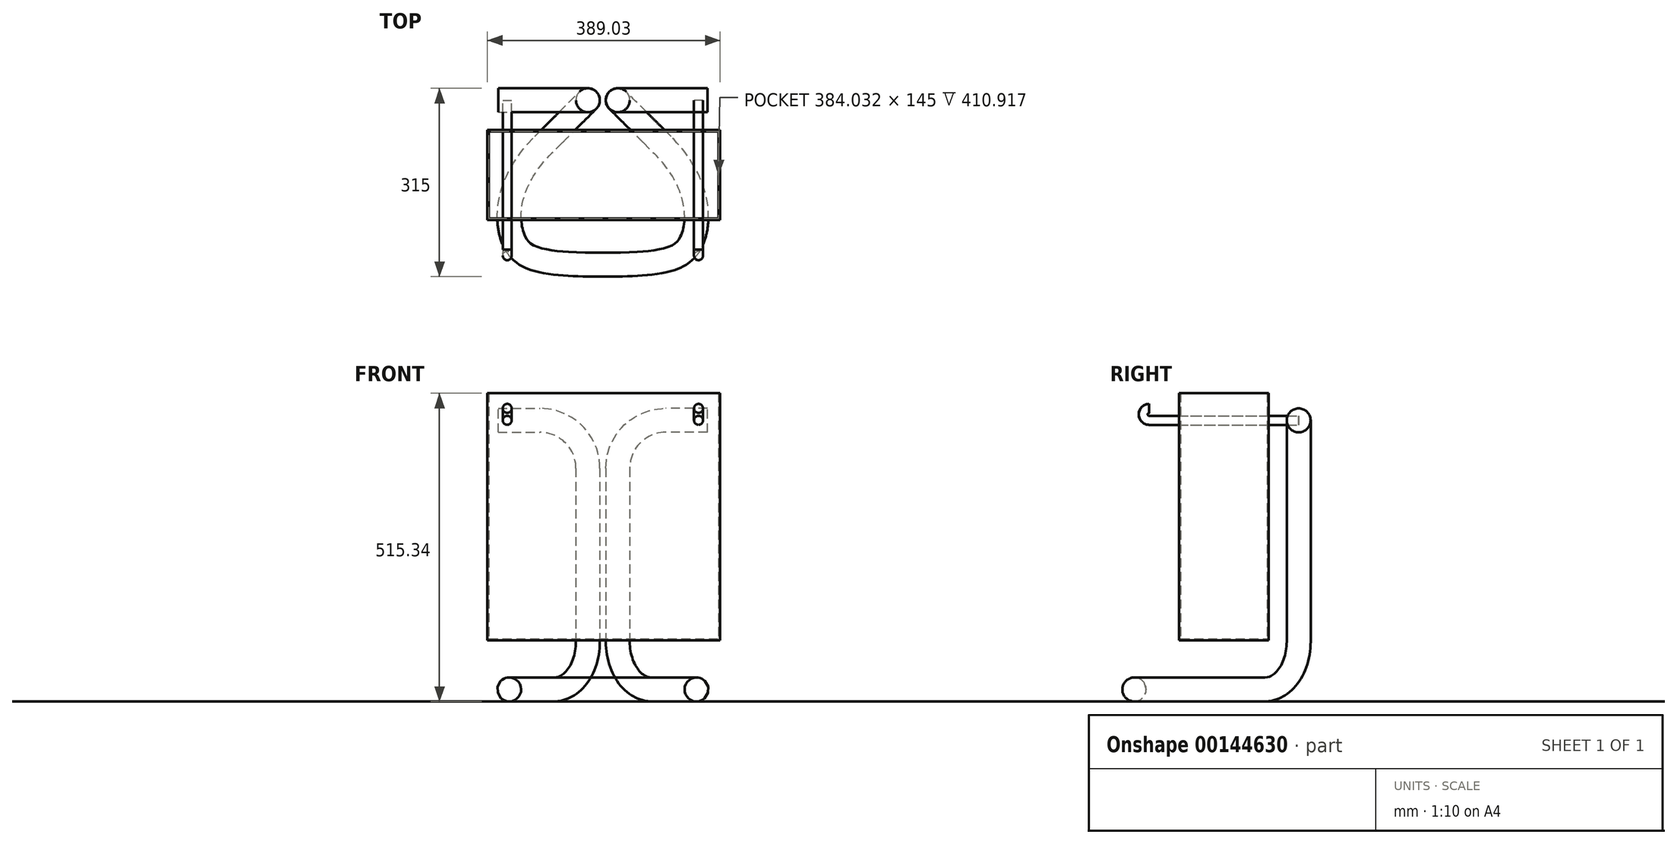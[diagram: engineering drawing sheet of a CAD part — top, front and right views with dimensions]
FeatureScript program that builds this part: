
annotation { "Feature Type Name" : "Feature", "Feature Type Description" : "" }
export const myFeature = defineFeature(function(context is Context, id is Id, definition is map)
    precondition{}
    {
        {
            var Q0;
            Q0=qCreatedBy(makeId("Top.planeOp"),FACE);
            var sketch = newSketch(context, id + "F0", { "sketchPlane" : qUnion([Q0])});
            skLineSegment(sketch, "E0.bottom", {"start": v(-150, 150) * mm, "end": v(150, 150) * mm, "construction": true});
            skLineSegment(sketch, "E0.top", {"start": v(-150, -150) * mm, "end": v(150, -150) * mm, "construction": true});
            skLineSegment(sketch, "E0.left", {"start": v(-150, 150) * mm, "end": v(-150, -150) * mm, "construction": true});
            skLineSegment(sketch, "E0.right", {"start": v(150, 150) * mm, "end": v(150, -150) * mm, "construction": true});
            skPoint(sketch, "E0.middle", {"position": v(0, 0) * mm});
            skLineSegment(sketch, "E1", {"start": v(0, 150) * mm, "end": v(0, -150) * mm, "construction": true});
            skFitSpline(sketch, "E2", {"points": [v(0, -150) * mm, v(150, -106.6) * mm, v(100, 50) * mm], "startDerivative": vector(649.1, 0) * mm, "endDerivative": vector(-356.53, 356.53) * mm});
            skLineSegment(sketch, "E3", {"start": v(0, 50) * mm, "end": v(100, 50) * mm, "construction": true});
            skLineSegment(sketch, "E4", {"start": v(100, 50) * mm, "end": v(100, 150) * mm, "construction": true});
            skLineSegment(sketch, "E5", {"start": v(0, 150) * mm, "end": v(187.01, -37.01) * mm, "construction": true});
            skCircle(sketch, "E6", {"center": v(25, 125) * mm, "radius": 25 * mm});
            skLineSegment(sketch, "E7", {"start": v(25, 125) * mm, "end": v(150, 125) * mm, "construction": true});
            skSolve(sketch);
        }
        {
            var Q0;
            Q0=qCreatedBy(makeId("Right.planeOp"),FACE);
            var sketch = newSketch(context, id + "F1", { "sketchPlane" : qUnion([Q0])});
            skLineSegment(sketch, "E8", {"start": v(150, 0) * mm, "end": v(150, 128.92) * mm});
            skSolve(sketch);
        }
        {
            var Q0;
            Q0=sQuery(id+"F1.wireOp",VERTEX,"E8.end");
            var Q1;
            Q1=sQuery(id+"F1.wireOp",VERTEX,"E8.start");
            var Q2;
            Q2=sQuery(id+"F0.wireOp",VERTEX,"E4.start");
            cPlane(context, id + "F2", {"entities" : qUnion([Q0, Q1, Q2]), "cplaneType" : CPlaneType.THREE_POINT, "offset" : 25 * mm, "width" : 150 * mm, "height" : 150 * mm});
        }
        {
            var Q0;
            Q0=qCreatedBy(id+"F2.planeOp",FACE);
            var sketch = newSketch(context, id + "F3", { "sketchPlane" : qUnion([Q0])});
            skLineSegment(sketch, "E9", {"start": v(70.71, 80) * mm, "end": v(70.71, 450) * mm});
            skLineSegment(sketch, "E10", {"start": v(-35.36, 0) * mm, "end": v(-9.29, 0) * mm});
            skPoint(sketch, "E11.visualSharp", {"position": v(70.71, 0) * mm});
            skArc(sketch, "E11.filletArc", {"start": v(-9.29, 0) * mm, "mid": v(47.28, 23.43) * mm, "end": v(70.71, 80) * mm});
            skSolve(sketch);
        }
        {
            var Q0;
            Q0=sQuery(id+"F0.wireOp",VERTEX,"E7.end");
            var Q1;
            Q1=sQuery(id+"F3.wireOp",VERTEX,"E11.visualSharp");
            var Q2;
            Q2=sQuery(id+"F3.wireOp",VERTEX,"E9.end");
            cPlane(context, id + "F4", {"entities" : qUnion([Q0, Q1, Q2]), "cplaneType" : CPlaneType.THREE_POINT, "offset" : 25 * mm, "width" : 150 * mm, "height" : 150 * mm});
        }
        {
            var Q0;
            Q0=qCreatedBy(id+"F4.planeOp",FACE);
            var sketch = newSketch(context, id + "F5", { "sketchPlane" : qUnion([Q0])});
            skLineSegment(sketch, "E12", {"start": v(105, 450) * mm, "end": v(175, 450) * mm});
            skLineSegment(sketch, "E13", {"start": v(25, 370) * mm, "end": v(25, 80) * mm});
            skPoint(sketch, "E14.visualSharp", {"position": v(25, 450) * mm});
            skArc(sketch, "E14.filletArc", {"start": v(105, 450) * mm, "mid": v(48.43, 426.57) * mm, "end": v(25, 370) * mm});
            skSolve(sketch);
        }
        {
            var Q0;
            Q0=sQuery(id+"F5.wireOp",VERTEX,"E12.end");
            var Q1;
            Q1=sQuery(id+"F5.wireOp",EDGE,"E12");
            cPlane(context, id + "F6", {"entities" : qUnion([Q0, Q1]), "cplaneType" : CPlaneType.LINE_POINT, "offset" : 25 * mm, "width" : 150 * mm, "height" : 150 * mm});
        }
        {
            var Q0;
            Q0=qCreatedBy(id+"F6.planeOp",FACE);
            var sketch = newSketch(context, id + "F7", { "sketchPlane" : qUnion([Q0])});
            skCircle(sketch, "E15", {"center": v(125, 450) * mm, "radius": 20 * mm});
            skSolve(sketch);
        }
        {
            var Q0;
            Q0=makeQuery(id+"F7.imprint","IMPRINT",FACE,{"disambiguationData":[TD([[makeQuery(id+"F7.imprint","IMPRINT",EDGE,{"derivedFrom":sQuery(id+"F7.wireOp",EDGE,"E15")}),1.0]])]});
            var Q1;
            Q1=sQuery(id+"F5.wireOp",EDGE,"E12");
            var Q2;
            Q2=sQuery(id+"F5.wireOp",EDGE,"E14.filletArc");
            var Q3;
            Q3=sQuery(id+"F5.wireOp",EDGE,"E13");
            var Q4;
            Q4=sQuery(id+"F3.wireOp",EDGE,"E11.filletArc");
            var Q5;
            Q5=sQuery(id+"F3.wireOp",EDGE,"E10");
            var Q6;
            Q6=sQuery(id+"F0.wireOp",EDGE,"E2");
            sweep(context, id + "F8", {"profiles" : qUnion([Q0]), "path" : qUnion([Q1, Q2, Q3, Q4, Q5, Q6])});
        }
        {
            var Q0;
            Q0=makeQuery(id+"F8.opSweep","SWEPT_BODY",BODY,{"disambiguationData":[OSD([sQuery(id+"F0.wireOp",EDGE,"E2"),sQuery(id+"F7.wireOp",EDGE,"E15")])]});
            var Q1;
            Q1=qCreatedBy(makeId("Right.planeOp"),FACE);
            mirror(context, id + "F9", {"operationType" : NewBodyOperationType.ADD, "entities" : qUnion([Q0]), "mirrorPlane" : qUnion([Q1])});
        }
        {
            var Q0;
            Q0=qCreatedBy(id+"F4.planeOp",FACE);
            var sketch = newSketch(context, id + "F10", { "sketchPlane" : qUnion([Q0])});
            skLineSegment(sketch, "E16", {"start": v(0, 450) * mm, "end": v(279.79, 450) * mm, "construction": true});
            skCircle(sketch, "E17", {"center": v(160, 450) * mm, "radius": 7.5 * mm});
            skSolve(sketch);
        }
        {
            var Q0;
            Q0 = qSketchRegion(id + "F10", true);
            extrude(context, id + "F11", {"entities" : qUnion([Q0]), "depth" : 250 * mm});
        }
        {
            var Q0;
            Q0=qCreatedBy(makeId("Right.planeOp"),FACE);
            cPlane(context, id + "F12", {"entities" : qUnion([Q0]), "cplaneType" : CPlaneType.OFFSET, "offset" : 160 * mm, "width" : 150 * mm, "height" : 150 * mm});
        }
        {
            var Q0;
            Q0=makeQuery(id+"F11.opExtrude","CAP_FACE",FACE,{"disambiguationData":[OSD([sQuery(id+"F10.wireOp",EDGE,"E17")])],"isStart":false});
            var sketch = newSketch(context, id + "F13", { "sketchPlane" : qUnion([Q0])});
            skCircle(sketch, "E18", {"center": v(160, 450) * mm, "radius": 7.5 * mm});
            skLineSegment(sketch, "E19", {"start": v(160, 450) * mm, "end": v(160, 470) * mm, "construction": true});
            skCircle(sketch, "E20", {"center": v(160, 470) * mm, "radius": 2.5 * mm});
            skSolve(sketch);
        }
        {
            var Q0;
            Q0=qCreatedBy(id+"F12.planeOp",FACE);
            var sketch = newSketch(context, id + "F14", { "sketchPlane" : qUnion([Q0])});
            skLineSegment(sketch, "E21", {"start": v(-125, 450) * mm, "end": v(-125, 470) * mm, "construction": true});
            skArc(sketch, "E22", {"start": v(-125, 470) * mm, "mid": v(-135, 460) * mm, "end": v(-125, 450) * mm});
            skSolve(sketch);
        }
        {
            var Q0;
            Q0=makeQuery(id+"F13.imprint","IMPRINT",FACE,{"disambiguationData":[TD([[makeQuery(id+"F13.imprint","IMPRINT",EDGE,{"derivedFrom":sQuery(id+"F13.wireOp",EDGE,"E18")}),1.0]])]});
            var Q1;
            Q1=sQuery(id+"F14.wireOp",EDGE,"E22");
            sweep(context, id + "F15", {"operationType" : NewBodyOperationType.ADD, "profiles" : qUnion([Q0]), "path" : qUnion([Q1])});
        }
        {
            var Q0;
            Q0=makeQuery(id+"F11.opExtrude","SWEPT_BODY",BODY,{"disambiguationData":[OSD([sQuery(id+"F10.wireOp",EDGE,"E17")])]});
            var Q1;
            Q1=qCreatedBy(makeId("Right.planeOp"),FACE);
            mirror(context, id + "F16", {"entities" : qUnion([Q0]), "mirrorPlane" : qUnion([Q1])});
        }
        {
            var Q0;
            Q0=qCreatedBy(makeId("Front.planeOp"),FACE);
            var sketch = newSketch(context, id + "F17", { "sketchPlane" : qUnion([Q0])});
            skLineSegment(sketch, "E23.bottom", {"start": v(-193.02, 495.34) * mm, "end": v(196.01, 495.34) * mm});
            skLineSegment(sketch, "E23.top", {"start": v(-193.02, 81.92) * mm, "end": v(196.01, 81.92) * mm});
            skLineSegment(sketch, "E23.left", {"start": v(-193.02, 495.34) * mm, "end": v(-193.02, 81.92) * mm});
            skLineSegment(sketch, "E23.right", {"start": v(196.01, 495.34) * mm, "end": v(196.01, 81.92) * mm});
            skSolve(sketch);
        }
        {
            var Q0;
            Q0 = qSketchRegion(id + "F17", true);
            extrude(context, id + "F18", {"entities" : qUnion([Q0]), "endBound" : BoundingType.SYMMETRIC, "depth" : 150 * mm});
        }
        {
            var Q0;
            Q0=makeQuery(id+"F18.opExtrude","SWEPT_FACE",FACE,{"disambiguationData":[OSD([sQuery(id+"F17.wireOp",EDGE,"E23.bottom")])]});
            shell(context, id + "F19", {"entities" : qUnion([Q0]), "thickness" : 2.5 * mm});
        }
    });
